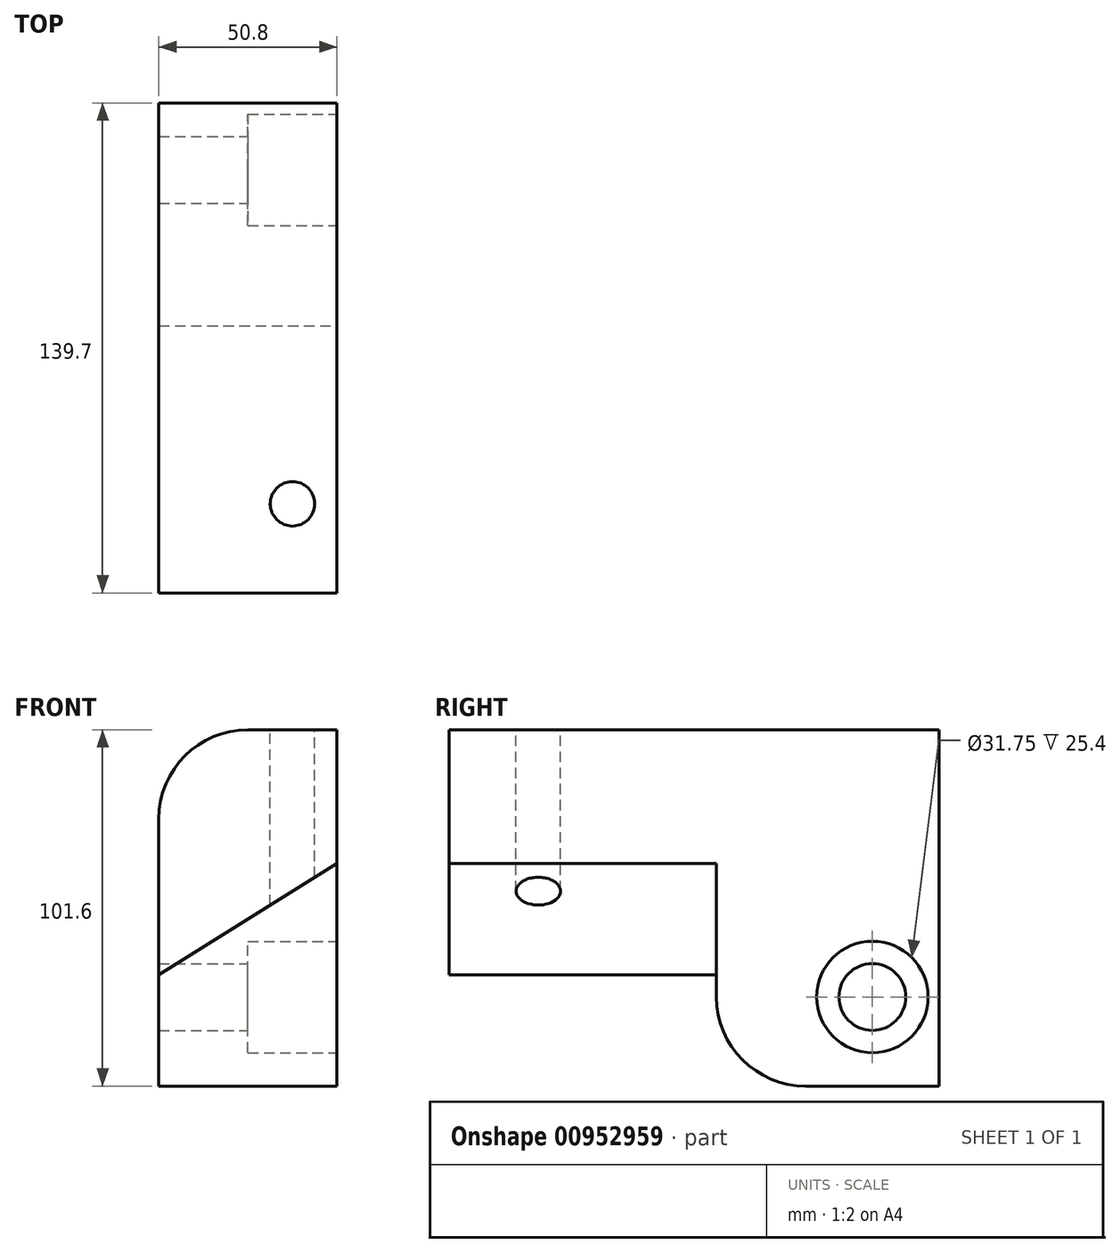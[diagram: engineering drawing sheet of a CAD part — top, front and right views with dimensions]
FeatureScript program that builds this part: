
annotation { "Feature Type Name" : "Feature", "Feature Type Description" : "" }
export const myFeature = defineFeature(function(context is Context, id is Id, definition is map)
    precondition{}
    {
        {
            var Q0;
            Q0=qCreatedBy(makeId("Front.planeOp"),FACE);
            var sketch = newSketch(context, id + "F0", { "sketchPlane" : qUnion([Q0])});
            skLineSegment(sketch, "E0.bottom", {"start": v(0, 50.8) * mm, "end": v(25.4, 50.8) * mm});
            skLineSegment(sketch, "E0.top", {"start": v(-25.4, -50.8) * mm, "end": v(25.4, -50.8) * mm});
            skLineSegment(sketch, "E0.left", {"start": v(-25.4, 25.4) * mm, "end": v(-25.4, -50.8) * mm});
            skLineSegment(sketch, "E0.right", {"start": v(25.4, 50.8) * mm, "end": v(25.4, -50.8) * mm});
            skPoint(sketch, "E0.middle", {"position": v(0, 0) * mm});
            skLineSegment(sketch, "E1", {"start": v(-25.4, -25.4) * mm, "end": v(25.4, -25.4) * mm});
            skLineSegment(sketch, "E2", {"start": v(-25.4, -19.05) * mm, "end": v(25.4, 12.7) * mm});
            skPoint(sketch, "E3.visualSharp", {"position": v(-25.4, 50.8) * mm});
            skArc(sketch, "E3.filletArc", {"start": v(0, 50.8) * mm, "mid": v(-17.96, 43.36) * mm, "end": v(-25.4, 25.4) * mm});
            skSolve(sketch);
        }
        {
            var Q0;
            Q0 = qSketchRegion(id + "F0", true);
            extrude(context, id + "F1", {"entities" : qUnion([Q0]), "depth" : 63.5 * mm, "offsetDistance" : 25.4 * mm});
        }
        {
            var Q0;
            {var subQ4=sQuery(id+"F0.wireOp",EDGE,"E0.bottom");Q0=makeQuery(id+"F0.imprint","IMPRINT",FACE,{"disambiguationData":[TD([[makeQuery(id+"F0.imprint","IMPRINT",EDGE,{"derivedFrom":subQ4}),-1.0]])]});}
            extrude(context, id + "F2", {"entities" : qUnion([Q0]), "operationType" : NewBodyOperationType.ADD, "depth" : 139.7 * mm, "offsetDistance" : 25.4 * mm});
        }
        {
            var Q0;
            Q0=makeQuery(id+"F1.opExtrude","CAP_EDGE",EDGE,{"disambiguationData":[OSD([sQuery(id+"F0.wireOp",EDGE,"E0.top")])],"isStart":false});
            fillet(context, id + "F3", {"entities" : qUnion([Q0]), "radius" : 25.4 * mm, "tangentPropagation" : true, "allowEdgeOverflow" : false});
        }
        {
            var Q0;
            {var subQ0=sQuery(id+"F0.wireOp",EDGE,"E0.right");Q0=makeQuery(id+"F2.boolean.opBoolean","MERGE",FACE,{"derivedFrom":[makeQuery(id+"F1.opExtrude","SWEPT_FACE",FACE,{"disambiguationData":[OSD([subQ0])]}),makeQuery(id+"F2.opExtrude","SWEPT_FACE",FACE,{"disambiguationData":[OSD([subQ0])]})]});}
            var sketch = newSketch(context, id + "F4", { "sketchPlane" : qUnion([Q0])});
            skPoint(sketch, "E4", {"position": v(-19.05, -25.4) * mm});
            skSolve(sketch);
        }
        {
            var Q0;
            Q0=sQuery(id+"F4.wireOp",VERTEX,"E4");
            var Q1;
            Q1=makeQuery(id+"F1.opExtrude","SWEPT_BODY",BODY,{"disambiguationData":[OSD([sQuery(id+"F0.wireOp",EDGE,"E0.bottom"),sQuery(id+"F0.wireOp",EDGE,"E0.top"),sQuery(id+"F0.wireOp",EDGE,"E0.left"),sQuery(id+"F0.wireOp",EDGE,"E0.right"),sQuery(id+"F0.wireOp",EDGE,"E3.filletArc")])]});
            hole(context, id + "F5", {"style" : HoleStyle.C_BORE, "endStyle" : HoleEndStyle.THROUGH, "holeDiameter" : 19.05 * mm, "cBoreDiameter" : 31.75 * mm, "cBoreDepth" : 25.4 * mm, "majorDiameter" : 6.35 * mm, "isTappedThrough" : true, "tappedDepth" : 12.7 * mm, "tapClearance" : 3, "startFromSketch" : true, "locations" : qUnion([Q0]), "scope" : qUnion([Q1])});
        }
        {
            var Q0;
            {var subQ0=sQuery(id+"F0.wireOp",EDGE,"E0.bottom");Q0=makeQuery(id+"F2.boolean.opBoolean","MERGE",FACE,{"derivedFrom":[makeQuery(id+"F1.opExtrude","SWEPT_FACE",FACE,{"disambiguationData":[OSD([subQ0])]}),makeQuery(id+"F2.opExtrude","SWEPT_FACE",FACE,{"disambiguationData":[OSD([subQ0])]})]});}
            var sketch = newSketch(context, id + "F6", { "sketchPlane" : qUnion([Q0])});
            skPoint(sketch, "E5", {"position": v(12.7, -114.3) * mm});
            skSolve(sketch);
        }
        {
            var Q0;
            Q0=sQuery(id+"F6.wireOp",VERTEX,"E5");
            var Q1;
            Q1=makeQuery(id+"F1.opExtrude","SWEPT_BODY",BODY,{"disambiguationData":[OSD([sQuery(id+"F0.wireOp",EDGE,"E0.bottom"),sQuery(id+"F0.wireOp",EDGE,"E0.top"),sQuery(id+"F0.wireOp",EDGE,"E0.left"),sQuery(id+"F0.wireOp",EDGE,"E0.right"),sQuery(id+"F0.wireOp",EDGE,"E3.filletArc")])]});
            hole(context, id + "F7", {"style" : HoleStyle.SIMPLE, "endStyle" : HoleEndStyle.THROUGH, "holeDiameter" : 12.7 * mm, "majorDiameter" : 6.35 * mm, "isTappedThrough" : true, "tappedDepth" : 12.7 * mm, "tapClearance" : 3, "startFromSketch" : true, "locations" : qUnion([Q0]), "scope" : qUnion([Q1])});
        }
    });
